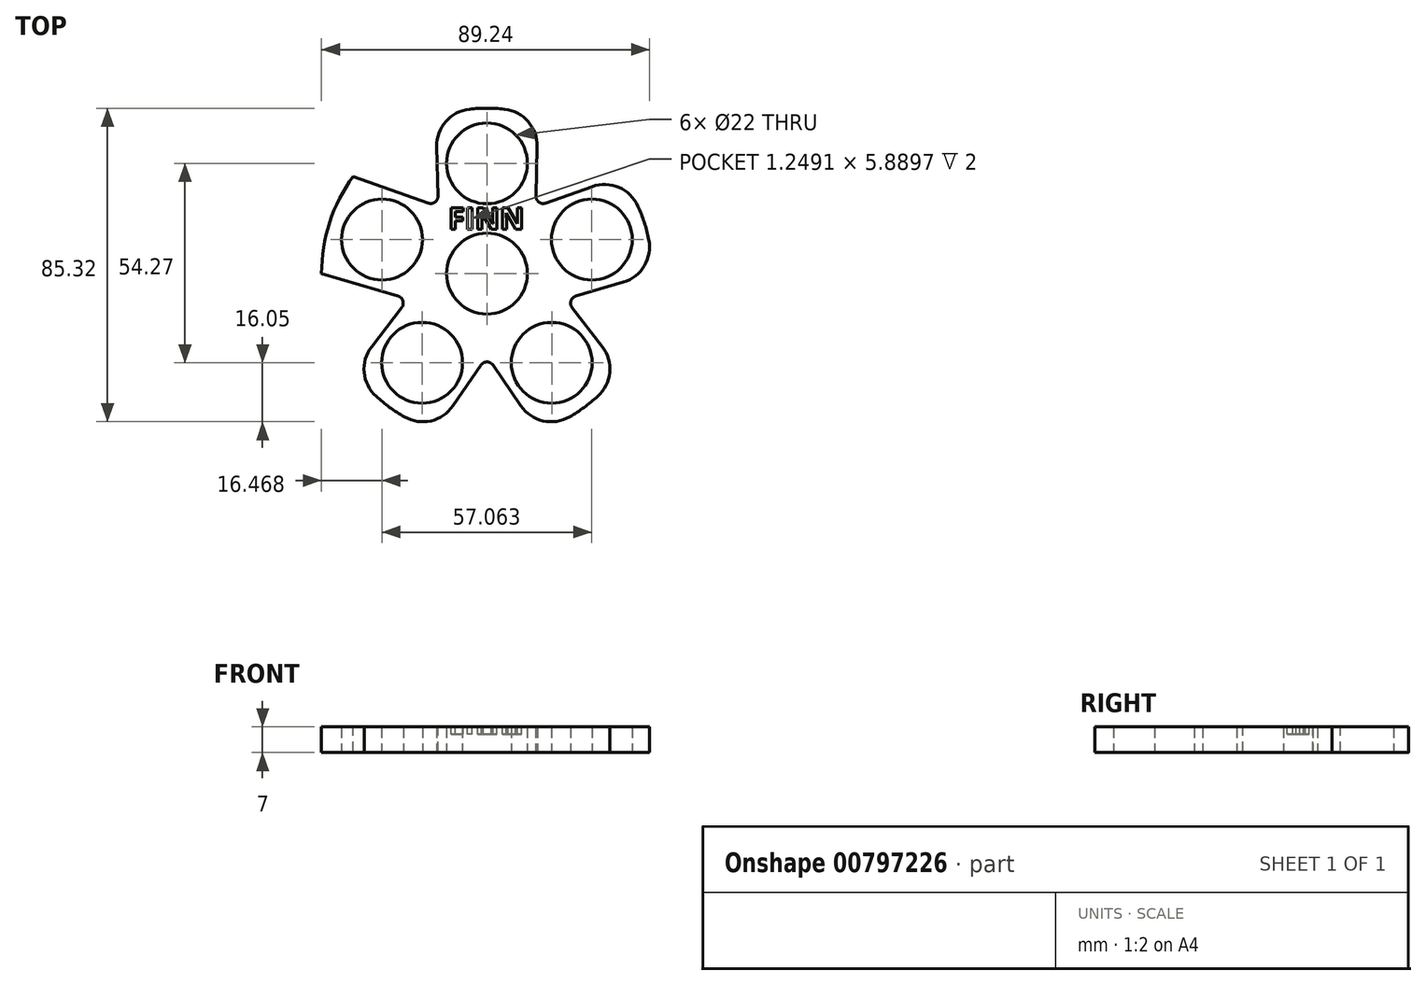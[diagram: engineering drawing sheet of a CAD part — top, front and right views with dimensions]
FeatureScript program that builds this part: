
annotation { "Feature Type Name" : "Feature", "Feature Type Description" : "" }
export const myFeature = defineFeature(function(context is Context, id is Id, definition is map)
    precondition{}
    {
        {
            var Q0;
            Q0=qCreatedBy(makeId("Top.planeOp"),FACE);
            var sketch = newSketch(context, id + "F0", { "sketchPlane" : qUnion([Q0])});
            skCircle(sketch, "E0", {"center": v(0, 0) * mm, "radius": 11 * mm});
            skCircle(sketch, "E1", {"center": v(28.53, 9.27) * mm, "radius": 11 * mm});
            skCircle(sketch, "E2", {"center": v(0, 30) * mm, "radius": 11 * mm});
            skCircle(sketch, "E3", {"center": v(17.63, -24.27) * mm, "radius": 11 * mm});
            skCircle(sketch, "E4", {"center": v(-17.63, -24.27) * mm, "radius": 11 * mm});
            skCircle(sketch, "E5", {"center": v(-28.53, 9.27) * mm, "radius": 11 * mm});
            skCircle(sketch, "E6", {"center": v(0, 0) * mm, "radius": 30 * mm, "construction": true});
            skLineSegment(sketch, "E7.0", {"start": v(0, 30) * mm, "end": v(28.53, 9.27) * mm, "construction": true});
            skLineSegment(sketch, "E7.1", {"start": v(28.53, 9.27) * mm, "end": v(17.63, -24.27) * mm, "construction": true});
            skLineSegment(sketch, "E7.2", {"start": v(17.63, -24.27) * mm, "end": v(-17.63, -24.27) * mm, "construction": true});
            skLineSegment(sketch, "E7.3", {"start": v(-17.63, -24.27) * mm, "end": v(-28.53, 9.27) * mm, "construction": true});
            skLineSegment(sketch, "E7.4", {"start": v(-28.53, 9.27) * mm, "end": v(0, 30) * mm, "construction": true});
            skCircle(sketch, "E8", {"center": v(0, 0) * mm, "radius": 45 * mm});
            skSolve(sketch);
        }
        {
            var Q0;
            Q0=makeQuery(id+"F0.imprint","IMPRINT",FACE,{"disambiguationData":[TD([[makeQuery(id+"F0.imprint","IMPRINT",EDGE,{"derivedFrom":sQuery(id+"F0.wireOp",EDGE,"E0")}),-1.0]])]});
            extrude(context, id + "F1", {"entities" : qUnion([Q0]), "depth" : 7 * mm, "offsetDistance" : 25 * mm});
        }
        {
            var Q0;
            Q0=makeQuery(id+"F1.opExtrude","CAP_FACE",FACE,{"disambiguationData":[OSD([sQuery(id+"F0.wireOp",EDGE,"E0"),sQuery(id+"F0.wireOp",EDGE,"E1"),sQuery(id+"F0.wireOp",EDGE,"E2"),sQuery(id+"F0.wireOp",EDGE,"E3"),sQuery(id+"F0.wireOp",EDGE,"E4"),sQuery(id+"F0.wireOp",EDGE,"E5"),sQuery(id+"F0.wireOp",EDGE,"E8")])],"isStart":false});
            var sketch = newSketch(context, id + "F2", { "sketchPlane" : qUnion([Q0])});
            skCircle(sketch, "E9.cCircle", {"center": v(0, 0) * mm, "radius": 45 * mm, "construction": true});
            skLineSegment(sketch, "E9.0", {"start": v(0, 45) * mm, "end": v(13.9, 42.8) * mm, "construction": true});
            skLineSegment(sketch, "E9.1", {"start": v(13.9, 42.8) * mm, "end": v(26.45, 36.4) * mm, "construction": true});
            skLineSegment(sketch, "E9.2", {"start": v(26.45, 36.4) * mm, "end": v(36.4, 26.45) * mm, "construction": true});
            skLineSegment(sketch, "E9.3", {"start": v(36.4, 26.45) * mm, "end": v(42.8, 13.9) * mm, "construction": true});
            skLineSegment(sketch, "E9.4", {"start": v(42.8, 13.9) * mm, "end": v(45, 0) * mm, "construction": true});
            skLineSegment(sketch, "E9.5", {"start": v(45, 0) * mm, "end": v(42.8, -13.9) * mm, "construction": true});
            skLineSegment(sketch, "E9.6", {"start": v(42.8, -13.9) * mm, "end": v(36.4, -26.45) * mm, "construction": true});
            skLineSegment(sketch, "E9.7", {"start": v(36.4, -26.45) * mm, "end": v(26.45, -36.4) * mm, "construction": true});
            skLineSegment(sketch, "E9.8", {"start": v(26.45, -36.4) * mm, "end": v(13.9, -42.8) * mm, "construction": true});
            skLineSegment(sketch, "E9.9", {"start": v(13.9, -42.8) * mm, "end": v(0, -45) * mm, "construction": true});
            skLineSegment(sketch, "E9.10", {"start": v(0, -45) * mm, "end": v(-13.9, -42.8) * mm, "construction": true});
            skLineSegment(sketch, "E9.11", {"start": v(-13.9, -42.8) * mm, "end": v(-26.45, -36.4) * mm, "construction": true});
            skLineSegment(sketch, "E9.12", {"start": v(-26.45, -36.4) * mm, "end": v(-36.4, -26.45) * mm, "construction": true});
            skLineSegment(sketch, "E9.13", {"start": v(-36.4, -26.45) * mm, "end": v(-42.8, -13.9) * mm, "construction": true});
            skLineSegment(sketch, "E9.14", {"start": v(-42.8, -13.9) * mm, "end": v(-45, 0) * mm, "construction": true});
            skLineSegment(sketch, "E9.15", {"start": v(-45, 0) * mm, "end": v(-42.8, 13.9) * mm, "construction": true});
            skLineSegment(sketch, "E9.16", {"start": v(-42.8, 13.9) * mm, "end": v(-36.4, 26.45) * mm, "construction": true});
            skLineSegment(sketch, "E9.17", {"start": v(-36.4, 26.45) * mm, "end": v(-26.45, 36.4) * mm, "construction": true});
            skLineSegment(sketch, "E9.18", {"start": v(-26.45, 36.4) * mm, "end": v(-13.9, 42.8) * mm, "construction": true});
            skLineSegment(sketch, "E9.19", {"start": v(-13.9, 42.8) * mm, "end": v(0, 45) * mm, "construction": true});
            skCircle(sketch, "E10", {"center": v(0, 0) * mm, "radius": 22.5 * mm, "construction": true});
            skLineSegment(sketch, "E11.0", {"start": v(0, 22.5) * mm, "end": v(13.23, 18.2) * mm, "construction": true});
            skLineSegment(sketch, "E11.1", {"start": v(13.23, 18.2) * mm, "end": v(21.4, 6.95) * mm, "construction": true});
            skLineSegment(sketch, "E11.2", {"start": v(21.4, 6.95) * mm, "end": v(21.4, -6.95) * mm, "construction": true});
            skLineSegment(sketch, "E11.3", {"start": v(21.4, -6.95) * mm, "end": v(13.23, -18.2) * mm, "construction": true});
            skLineSegment(sketch, "E11.4", {"start": v(13.23, -18.2) * mm, "end": v(0, -22.5) * mm, "construction": true});
            skLineSegment(sketch, "E11.5", {"start": v(0, -22.5) * mm, "end": v(-13.23, -18.2) * mm, "construction": true});
            skLineSegment(sketch, "E11.6", {"start": v(-13.23, -18.2) * mm, "end": v(-21.4, -6.95) * mm, "construction": true});
            skLineSegment(sketch, "E11.7", {"start": v(-21.4, -6.95) * mm, "end": v(-21.4, 6.95) * mm, "construction": true});
            skLineSegment(sketch, "E11.8", {"start": v(-21.4, 6.95) * mm, "end": v(-13.23, 18.2) * mm, "construction": true});
            skLineSegment(sketch, "E11.9", {"start": v(-13.23, 18.2) * mm, "end": v(0, 22.5) * mm, "construction": true});
            skLineSegment(sketch, "E12", {"start": v(13.9, 42.8) * mm, "end": v(13.23, 18.2) * mm});
            skLineSegment(sketch, "E13", {"start": v(13.23, 18.2) * mm, "end": v(36.4, 26.45) * mm});
            skLineSegment(sketch, "E14", {"start": v(-13.23, 18.2) * mm, "end": v(-13.9, 42.8) * mm});
            skLineSegment(sketch, "E15", {"start": v(-13.23, 18.2) * mm, "end": v(-36.4, 26.45) * mm});
            skLineSegment(sketch, "E16", {"start": v(-45, 0) * mm, "end": v(-21.4, -6.95) * mm});
            skLineSegment(sketch, "E17", {"start": v(-21.4, -6.95) * mm, "end": v(-36.4, -26.45) * mm});
            skLineSegment(sketch, "E18", {"start": v(-13.9, -42.8) * mm, "end": v(0, -22.5) * mm});
            skLineSegment(sketch, "E19", {"start": v(0, -22.5) * mm, "end": v(13.9, -42.8) * mm});
            skLineSegment(sketch, "E20", {"start": v(36.4, -26.45) * mm, "end": v(21.4, -6.95) * mm});
            skLineSegment(sketch, "E21", {"start": v(21.4, -6.95) * mm, "end": v(45, 0) * mm});
            skSolve(sketch);
        }
        {
            var Q0;
            {var subQ0=sQuery(id+"F2.wireOp",EDGE,"E14");Q0=makeQuery(id+"F2.imprint","IMPRINT",FACE,{"disambiguationData":[TD([[makeQuery(id+"F2.imprint","IMPRINT",EDGE,{"derivedFrom":subQ0}),1.0]])]});}
            var Q1;
            {var subQ0=sQuery(id+"F2.wireOp",EDGE,"E12");Q1=makeQuery(id+"F2.imprint","IMPRINT",FACE,{"disambiguationData":[TD([[makeQuery(id+"F2.imprint","IMPRINT",EDGE,{"derivedFrom":subQ0}),1.0]])]});}
            var Q2;
            {var subQ0=sQuery(id+"F2.wireOp",EDGE,"E20");Q2=makeQuery(id+"F2.imprint","IMPRINT",FACE,{"disambiguationData":[TD([[makeQuery(id+"F2.imprint","IMPRINT",EDGE,{"derivedFrom":subQ0}),-1.0]])]});}
            var Q3;
            {var subQ0=sQuery(id+"F2.wireOp",EDGE,"E18");Q3=makeQuery(id+"F2.imprint","IMPRINT",FACE,{"disambiguationData":[TD([[makeQuery(id+"F2.imprint","IMPRINT",EDGE,{"derivedFrom":subQ0}),-1.0]])]});}
            var Q4;
            {var subQ0=sQuery(id+"F2.wireOp",EDGE,"E16");Q4=makeQuery(id+"F2.imprint","IMPRINT",FACE,{"disambiguationData":[TD([[makeQuery(id+"F2.imprint","IMPRINT",EDGE,{"derivedFrom":subQ0}),-1.0]])]});}
            extrude(context, id + "F3", {"entities" : qUnion([Q0, Q1, Q2, Q3, Q4]), "operationType" : NewBodyOperationType.REMOVE, "oppositeDirection" : true, "depth" : 25 * mm, "offsetDistance" : 25 * mm});
        }
        {
            var Q0;
            Q0=makeQuery(id+"F3.boolean.opBoolean","COPY",EDGE,{"derivedFrom":makeQuery(id+"F3.opExtrude","SWEPT_EDGE",EDGE,{"disambiguationData":[OSD([sQuery(id+"F0.wireOp",EDGE,"E8"),sQuery(id+"F2.wireOp",EDGE,"E14")])]})});
            var Q1;
            Q1=makeQuery(id+"F3.boolean.opBoolean","COPY",EDGE,{"derivedFrom":makeQuery(id+"F3.opExtrude","SWEPT_EDGE",EDGE,{"disambiguationData":[OSD([sQuery(id+"F0.wireOp",EDGE,"E8"),sQuery(id+"F2.wireOp",EDGE,"E15")])]})});
            var Q2;
            Q2=makeQuery(id+"F3.boolean.opBoolean","COPY",EDGE,{"derivedFrom":makeQuery(id+"F3.opExtrude","SWEPT_EDGE",EDGE,{"disambiguationData":[OSD([sQuery(id+"F0.wireOp",EDGE,"E8"),sQuery(id+"F2.wireOp",EDGE,"E13")])]})});
            var Q3;
            Q3=makeQuery(id+"F3.boolean.opBoolean","COPY",EDGE,{"derivedFrom":makeQuery(id+"F3.opExtrude","SWEPT_EDGE",EDGE,{"disambiguationData":[OSD([sQuery(id+"F0.wireOp",EDGE,"E8"),sQuery(id+"F2.wireOp",EDGE,"E12")])]})});
            var Q4;
            Q4=makeQuery(id+"F3.boolean.opBoolean","COPY",EDGE,{"derivedFrom":makeQuery(id+"F3.opExtrude","SWEPT_EDGE",EDGE,{"disambiguationData":[OSD([sQuery(id+"F0.wireOp",EDGE,"E8"),sQuery(id+"F2.wireOp",EDGE,"E21")])]})});
            var Q5;
            Q5=makeQuery(id+"F3.boolean.opBoolean","COPY",EDGE,{"derivedFrom":makeQuery(id+"F3.opExtrude","SWEPT_EDGE",EDGE,{"disambiguationData":[OSD([sQuery(id+"F0.wireOp",EDGE,"E8"),sQuery(id+"F2.wireOp",EDGE,"E20")])]})});
            var Q6;
            Q6=makeQuery(id+"F3.boolean.opBoolean","COPY",EDGE,{"derivedFrom":makeQuery(id+"F3.opExtrude","SWEPT_EDGE",EDGE,{"disambiguationData":[OSD([sQuery(id+"F0.wireOp",EDGE,"E8"),sQuery(id+"F2.wireOp",EDGE,"E19")])]})});
            var Q7;
            Q7=makeQuery(id+"F3.boolean.opBoolean","COPY",EDGE,{"derivedFrom":makeQuery(id+"F3.opExtrude","SWEPT_EDGE",EDGE,{"disambiguationData":[OSD([sQuery(id+"F0.wireOp",EDGE,"E8"),sQuery(id+"F2.wireOp",EDGE,"E18")])]})});
            var Q8;
            Q8=makeQuery(id+"F3.boolean.opBoolean","COPY",EDGE,{"derivedFrom":makeQuery(id+"F3.opExtrude","SWEPT_EDGE",EDGE,{"disambiguationData":[OSD([sQuery(id+"F0.wireOp",EDGE,"E8"),sQuery(id+"F2.wireOp",EDGE,"E17")])]})});
            var Q9;
            Q9=makeQuery(id+"F3.boolean.opBoolean","COPY",EDGE,{"derivedFrom":makeQuery(id+"F3.opExtrude","SWEPT_EDGE",EDGE,{"disambiguationData":[OSD([sQuery(id+"F0.wireOp",EDGE,"E8"),sQuery(id+"F2.wireOp",EDGE,"E16")])]})});
            fillet(context, id + "F4", {"entities" : qUnion([Q0, Q1, Q2, Q3, Q4, Q5, Q6, Q7, Q8, Q9]), "radius" : 10 * mm, "tangentPropagation" : true, "allowEdgeOverflow" : false});
        }
        {
            var Q0;
            Q0=makeQuery(id+"F3.boolean.opBoolean","COPY",EDGE,{"derivedFrom":makeQuery(id+"F3.opExtrude","SWEPT_EDGE",EDGE,{"disambiguationData":[OSD([sQuery(id+"F2.wireOp",EDGE,"E12"),sQuery(id+"F2.wireOp",EDGE,"E13")])]})});
            var Q1;
            Q1=makeQuery(id+"F3.boolean.opBoolean","COPY",EDGE,{"derivedFrom":makeQuery(id+"F3.opExtrude","SWEPT_EDGE",EDGE,{"disambiguationData":[OSD([sQuery(id+"F2.wireOp",EDGE,"E20"),sQuery(id+"F2.wireOp",EDGE,"E21")])]})});
            var Q2;
            Q2=makeQuery(id+"F3.boolean.opBoolean","COPY",EDGE,{"derivedFrom":makeQuery(id+"F3.opExtrude","SWEPT_EDGE",EDGE,{"disambiguationData":[OSD([sQuery(id+"F2.wireOp",EDGE,"E18"),sQuery(id+"F2.wireOp",EDGE,"E19")])]})});
            var Q3;
            Q3=makeQuery(id+"F3.boolean.opBoolean","COPY",EDGE,{"derivedFrom":makeQuery(id+"F3.opExtrude","SWEPT_EDGE",EDGE,{"disambiguationData":[OSD([sQuery(id+"F2.wireOp",EDGE,"E16"),sQuery(id+"F2.wireOp",EDGE,"E17")])]})});
            var Q4;
            Q4=makeQuery(id+"F3.boolean.opBoolean","COPY",EDGE,{"derivedFrom":makeQuery(id+"F3.opExtrude","SWEPT_EDGE",EDGE,{"disambiguationData":[OSD([sQuery(id+"F2.wireOp",EDGE,"E14"),sQuery(id+"F2.wireOp",EDGE,"E15")])]})});
            fillet(context, id + "F5", {"entities" : qUnion([Q0, Q1, Q2, Q3, Q4]), "radius" : 2 * mm, "tangentPropagation" : true, "allowEdgeOverflow" : false});
        }
        {
            var Q0;
            Q0=makeQuery(id+"F1.opExtrude","CAP_FACE",FACE,{"disambiguationData":[OSD([sQuery(id+"F0.wireOp",EDGE,"E0"),sQuery(id+"F0.wireOp",EDGE,"E1"),sQuery(id+"F0.wireOp",EDGE,"E2"),sQuery(id+"F0.wireOp",EDGE,"E3"),sQuery(id+"F0.wireOp",EDGE,"E4"),sQuery(id+"F0.wireOp",EDGE,"E5"),sQuery(id+"F0.wireOp",EDGE,"E8")])],"isStart":false});
            var sketch = newSketch(context, id + "F6", { "sketchPlane" : qUnion([Q0])});
            skText(sketch, "E22", { "text": "FINN", "fontName": "OpenSans-Bold.ttf"});
            const initialGuessF6  = {"E22": [-0.01052, 0.01206, 1, 0, 0.00594]};
            skSetInitialGuess(sketch, initialGuessF6);
            skSolve(sketch);
        }
        {
            var Q0;
            Q0 = qSketchRegion(id + "F6", true);
            extrude(context, id + "F7", {"entities" : qUnion([Q0]), "operationType" : NewBodyOperationType.REMOVE, "oppositeDirection" : true, "depth" : 2 * mm, "offsetDistance" : 25 * mm});
        }
    });
